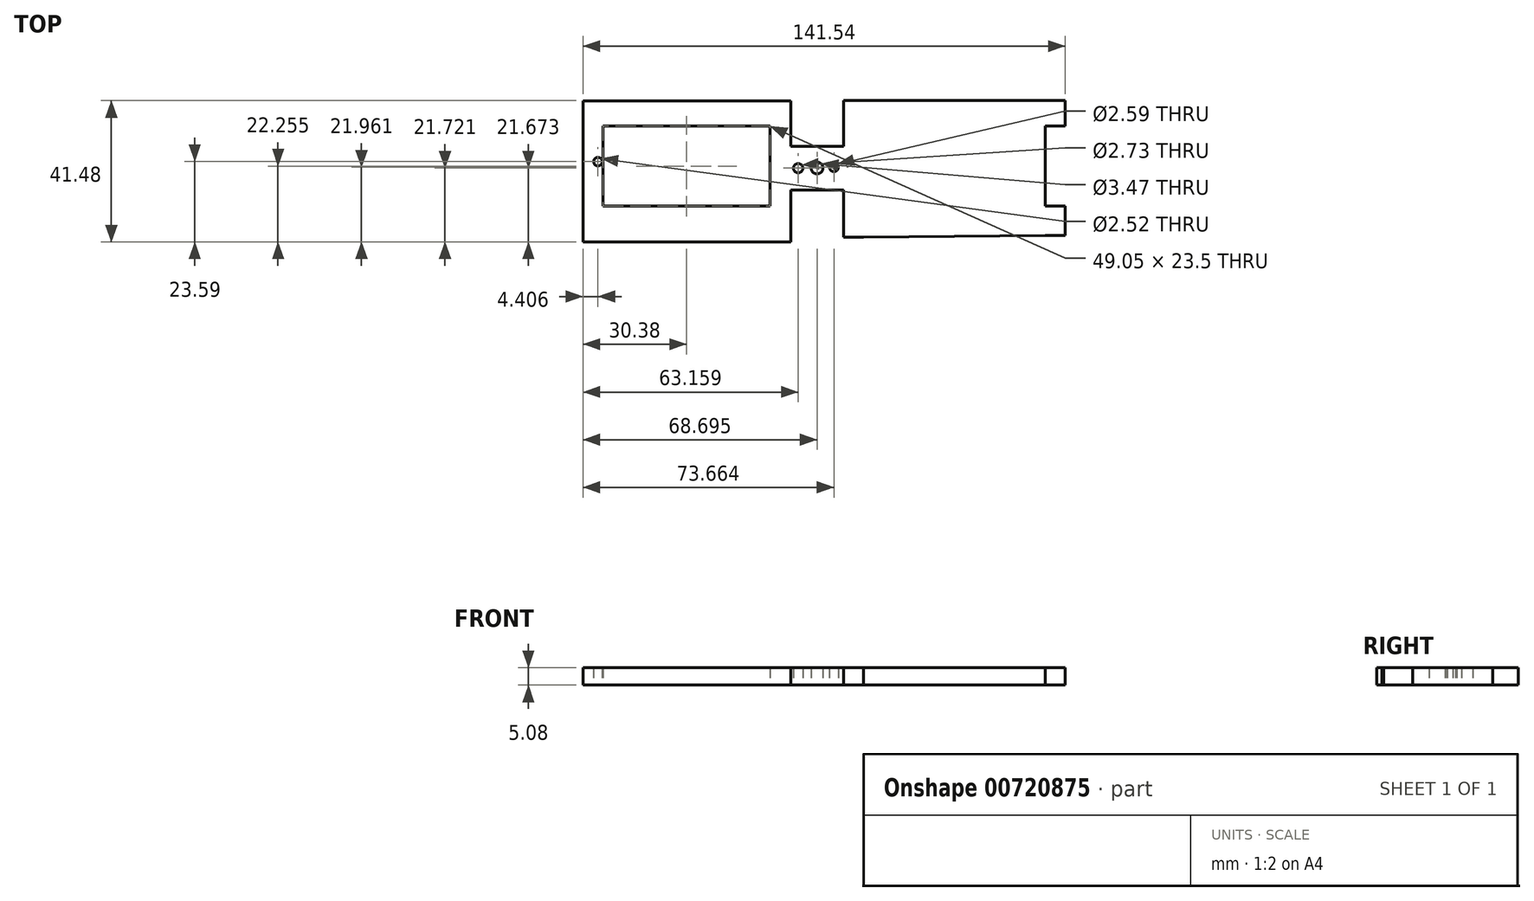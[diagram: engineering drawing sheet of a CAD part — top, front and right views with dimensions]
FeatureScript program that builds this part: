
annotation { "Feature Type Name" : "Feature", "Feature Type Description" : "" }
export const myFeature = defineFeature(function(context is Context, id is Id, definition is map)
    precondition{}
    {
        {
            var Q0;
            Q0=qCreatedBy(makeId("Top.planeOp"),FACE);
            var sketch = newSketch(context, id + "F0", { "sketchPlane" : qUnion([Q0])});
            skLineSegment(sketch, "E0.bottom", {"start": v(131.64, 10.41) * mm, "end": v(75.56, 10.41) * mm});
            skLineSegment(sketch, "E0.top", {"start": v(131.64, -13.08) * mm, "end": v(75.56, -13.08) * mm});
            skLineSegment(sketch, "E0.right", {"start": v(75.56, 10.41) * mm, "end": v(75.56, -13.08) * mm});
            skLineSegment(sketch, "E1.bottom", {"start": v(75.56, 10.41) * mm, "end": v(128.9, 10.41) * mm});
            skLineSegment(sketch, "E1.top", {"start": v(75.56, 17.89) * mm, "end": v(128.9, 17.89) * mm});
            skLineSegment(sketch, "E1.left", {"start": v(75.56, 10.41) * mm, "end": v(75.56, 17.89) * mm});
            skLineSegment(sketch, "E1.right", {"start": v(128.9, 10.41) * mm, "end": v(128.9, 17.89) * mm});
            skLineSegment(sketch, "E2.left", {"start": v(75.56, -13.08) * mm, "end": v(75.56, -20.56) * mm});
            skLineSegment(sketch, "E3.bottom", {"start": v(75.56, 17.89) * mm, "end": v(69.69, 17.89) * mm});
            skLineSegment(sketch, "E3.top", {"start": v(75.56, -22.16) * mm, "end": v(69.69, -22.16) * mm});
            skLineSegment(sketch, "E3.left", {"start": v(75.56, 17.89) * mm, "end": v(75.56, -22.16) * mm});
            skLineSegment(sketch, "E3.right", {"start": v(69.69, 17.89) * mm, "end": v(69.69, -22.16) * mm});
            skLineSegment(sketch, "E4.bottom", {"start": v(128.9, 17.89) * mm, "end": v(134.78, 17.89) * mm});
            skLineSegment(sketch, "E4.top", {"start": v(128.9, -21.63) * mm, "end": v(134.78, -21.63) * mm});
            skLineSegment(sketch, "E4.left", {"start": v(128.9, 17.89) * mm, "end": v(128.9, -21.63) * mm});
            skLineSegment(sketch, "E4.right", {"start": v(134.78, 17.89) * mm, "end": v(134.78, -21.63) * mm});
            skLineSegment(sketch, "E5", {"start": v(69.69, 4.54) * mm, "end": v(54.2, 4.54) * mm});
            skLineSegment(sketch, "E6", {"start": v(54.2, 4.54) * mm, "end": v(54.2, -8.28) * mm});
            skLineSegment(sketch, "E7", {"start": v(54.2, -8.28) * mm, "end": v(69.69, -8.28) * mm});
            skLineSegment(sketch, "E8", {"start": v(69.69, -8.28) * mm, "end": v(69.69, 4.54) * mm});
            skCircle(sketch, "E9", {"center": v(133.23, 0) * mm, "radius": 1.2 * mm});
            skCircle(sketch, "E10", {"center": v(61.93, -1.87) * mm, "radius": 1.74 * mm});
            skPoint(sketch, "E10.centerSnap0", {"position": v(69.69, -1.87) * mm});
            skPoint(sketch, "E10.perimeterSnap0", {"position": v(69.69, -1.87) * mm});
            skLineSegment(sketch, "E11.bottom", {"start": v(54.2, 17.8) * mm, "end": v(-6.76, 17.8) * mm});
            skLineSegment(sketch, "E11.top", {"start": v(54.2, -23.59) * mm, "end": v(-6.76, -23.59) * mm});
            skLineSegment(sketch, "E11.left", {"start": v(54.2, 17.8) * mm, "end": v(54.2, -23.59) * mm});
            skLineSegment(sketch, "E11.right", {"start": v(-6.76, 17.8) * mm, "end": v(-6.76, -23.59) * mm});
            skLineSegment(sketch, "E12", {"start": v(75.56, -22.16) * mm, "end": v(128.9, -21.63) * mm});
            skCircle(sketch, "E13", {"center": v(186.14, 0) * mm, "radius": 1.6 * mm});
            skLineSegment(sketch, "E14", {"start": v(54.2, 10.41) * mm, "end": v(-6.76, 10.41) * mm});
            skLineSegment(sketch, "E15", {"start": v(54.2, -13.08) * mm, "end": v(-6.76, -13.08) * mm});
            skLineSegment(sketch, "E16", {"start": v(75.56, 17.89) * mm, "end": v(75.56, 10.41) * mm});
            skLineSegment(sketch, "E17", {"start": v(54.2, 17.8) * mm, "end": v(48.14, 17.8) * mm});
            skLineSegment(sketch, "E18", {"start": v(48.14, 17.8) * mm, "end": v(48.14, -23.59) * mm});
            skLineSegment(sketch, "E19", {"start": v(48.14, -23.59) * mm, "end": v(54.2, -23.59) * mm});
            skLineSegment(sketch, "E20", {"start": v(-6.76, 17.8) * mm, "end": v(-0.9, 17.8) * mm});
            skLineSegment(sketch, "E21", {"start": v(-0.9, 17.8) * mm, "end": v(-0.9, -23.59) * mm});
            skLineSegment(sketch, "E22", {"start": v(-0.9, -23.59) * mm, "end": v(-6.76, -23.59) * mm});
            skLineSegment(sketch, "E23", {"start": v(75.56, -13.08) * mm, "end": v(134.78, -13.08) * mm});
            skLineSegment(sketch, "E24", {"start": v(134.78, -13.08) * mm, "end": v(75.56, -13.08) * mm});
            skLineSegment(sketch, "E25", {"start": v(131.64, 10.41) * mm, "end": v(134.78, 10.41) * mm});
            skCircle(sketch, "E26", {"center": v(-2.35, 0) * mm, "radius": 1.26 * mm});
            skCircle(sketch, "E27", {"center": v(66.9, -1.63) * mm, "radius": 1.3 * mm});
            skCircle(sketch, "E28", {"center": v(56.4, -1.92) * mm, "radius": 1.37 * mm});
            skSolve(sketch);
        }
        {
            var Q0;
            {var subQ0=sQuery(id+"F0.wireOp",EDGE,"E1.top");Q0=makeQuery(id+"F0.imprint","IMPRINT",FACE,{"disambiguationData":[TD([[makeQuery(id+"F0.imprint","IMPRINT",EDGE,{"derivedFrom":subQ0}),-1.0]])]});}
            var Q1;
            {var subQ3=sQuery(id+"F0.wireOp",EDGE,"E4.bottom");Q1=makeQuery(id+"F0.imprint","IMPRINT",FACE,{"disambiguationData":[TD([[makeQuery(id+"F0.imprint","IMPRINT",EDGE,{"derivedFrom":subQ3}),-1.0]])]});}
            var Q2;
            {var subQ0=sQuery(id+"F0.wireOp",EDGE,"E12");Q2=makeQuery(id+"F0.imprint","IMPRINT",FACE,{"disambiguationData":[TD([[makeQuery(id+"F0.imprint","IMPRINT",EDGE,{"derivedFrom":subQ0}),1.0]])]});}
            var Q3;
            {var subQ3=sQuery(id+"F0.wireOp",EDGE,"E3.bottom");Q3=makeQuery(id+"F0.imprint","IMPRINT",FACE,{"disambiguationData":[TD([[makeQuery(id+"F0.imprint","IMPRINT",EDGE,{"derivedFrom":subQ3}),1.0]])]});}
            extrude(context, id + "F1", {"entities" : qUnion([Q0, Q1, Q2, Q3]), "depth" : 5.08 * mm, "offsetDistance" : 25.4 * mm});
        }
        {
            var Q0;
            {var subQ1=sQuery(id+"F0.wireOp",EDGE,"E5");Q0=makeQuery(id+"F0.imprint","IMPRINT",FACE,{"disambiguationData":[TD([[makeQuery(id+"F0.imprint","IMPRINT",EDGE,{"derivedFrom":subQ1}),1.0]])]});}
            extrude(context, id + "F2", {"entities" : qUnion([Q0]), "operationType" : NewBodyOperationType.ADD, "depth" : 5.08 * mm, "offsetDistance" : 25.4 * mm});
        }
        {
            var Q0;
            {var subQ5=sQuery(id+"F0.wireOp",EDGE,"E0.bottom");Q0=makeQuery(id+"F0.imprint","IMPRINT",FACE,{"disambiguationData":[TD([[makeQuery(id+"F0.imprint","IMPRINT",EDGE,{"derivedFrom":subQ5}),1.0]])]});}
            var Q1;
            {var subQ4=sQuery(id+"F0.wireOp",EDGE,"E4.top");Q1=makeQuery(id+"F0.imprint","IMPRINT",FACE,{"disambiguationData":[TD([[makeQuery(id+"F0.imprint","IMPRINT",EDGE,{"derivedFrom":subQ4}),1.0]])]});}
            var Q2;
            {var subQ0=sQuery(id+"F0.wireOp",EDGE,"E19");Q2=makeQuery(id+"F0.imprint","IMPRINT",FACE,{"disambiguationData":[TD([[makeQuery(id+"F0.imprint","IMPRINT",EDGE,{"derivedFrom":subQ0}),1.0]])]});}
            var Q3;
            {var subQ0=sQuery(id+"F0.wireOp",EDGE,"E11.top");Q3=makeQuery(id+"F0.imprint","IMPRINT",FACE,{"disambiguationData":[TD([[makeQuery(id+"F0.imprint","IMPRINT",EDGE,{"derivedFrom":subQ0}),-1.0]])]});}
            var Q4;
            {var subQ1=sQuery(id+"F0.wireOp",EDGE,"E11.left");var subQ8=makeQuery(id+"F0.imprint","INTERSECT",VERTEX,{"derivedFrom":[sQuery(id+"F0.wireOp",EDGE,"E5"),subQ1]});Q4=makeQuery(id+"F0.imprint","IMPRINT",FACE,{"disambiguationData":[TD([[makeQuery(id+"F0.imprint","IMPRINT",EDGE,{"disambiguationData":[TD([[subQ8,1.0]])],"derivedFrom":subQ1}),-1.0]])]});}
            var Q5;
            {var subQ0=sQuery(id+"F0.wireOp",EDGE,"E17");Q5=makeQuery(id+"F0.imprint","IMPRINT",FACE,{"disambiguationData":[TD([[makeQuery(id+"F0.imprint","IMPRINT",EDGE,{"derivedFrom":subQ0}),1.0]])]});}
            var Q6;
            {var subQ0=sQuery(id+"F0.wireOp",EDGE,"E11.bottom");Q6=makeQuery(id+"F0.imprint","IMPRINT",FACE,{"disambiguationData":[TD([[makeQuery(id+"F0.imprint","IMPRINT",EDGE,{"derivedFrom":subQ0}),1.0]])]});}
            var Q7;
            {var subQ0=sQuery(id+"F0.wireOp",EDGE,"E20");Q7=makeQuery(id+"F0.imprint","IMPRINT",FACE,{"disambiguationData":[TD([[makeQuery(id+"F0.imprint","IMPRINT",EDGE,{"derivedFrom":subQ0}),-1.0]])]});}
            var Q8;
            {var subQ0=sQuery(id+"F0.wireOp",EDGE,"E22");Q8=makeQuery(id+"F0.imprint","IMPRINT",FACE,{"disambiguationData":[TD([[makeQuery(id+"F0.imprint","IMPRINT",EDGE,{"derivedFrom":subQ0}),-1.0]])]});}
            var Q9;
            Q9=makeQuery(id+"F0.imprint","IMPRINT",FACE,{"disambiguationData":[TD([[makeQuery(id+"F0.imprint","IMPRINT",EDGE,{"derivedFrom":sQuery(id+"F0.wireOp",EDGE,"E26")}),-1.0]])]});
            extrude(context, id + "F3", {"entities" : qUnion([Q0, Q1, Q2, Q3, Q4, Q5, Q6, Q7, Q8, Q9]), "operationType" : NewBodyOperationType.ADD, "depth" : 5.08 * mm, "offsetDistance" : 25.4 * mm});
        }
    });
